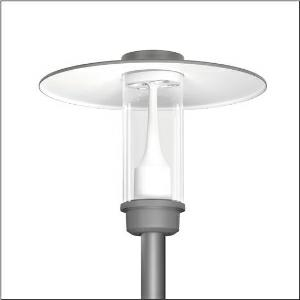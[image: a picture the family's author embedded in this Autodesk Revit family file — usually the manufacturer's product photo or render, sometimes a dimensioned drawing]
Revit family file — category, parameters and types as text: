
# Revit family: litepole_iq_2___p1_0a_5xa5425ff14h_b341
name_source: partatom
category: Lighting Fixtures
units: mm (PartAtom-declared; Revit-internal decimal feet)

## family parameters
Cut with Voids When Loaded = No
Host = Face
Light Source = No
Part Type = Normal
Room Calculation Point = No
Round Connector Dimension = Use Diameter
Shared = No

## types (1)
- --- (1 x LED, 1520 lm, 10.5 W, 3000K)
    Apparent Load = 11 VA
    CIE Flux Codes = 33 62 89 96 100
    Color Rendering = 70
    Color Temperature = 3000K
    Default Elevation = 1800 mm
    Description = Litepole iQ 2, mast luminaire, Module 540 iQ-SR, primary light control with 3 zone facetted reflector, of plastic, silver coated, highly specular, structured, primary optical cover: cover, of PMMA, transparent, light distribution: P1.0a, light emission: direct distribution, primary light characteristic: strongly asymmetric, installation type: post-top, LED, High Power LED, rated luminous flux: 1.520lm, luminous efficacy: 145lm/W, light colour: 730, colour temperature: 3000K, control gear: ECG iQ, control: Auto-Match, Temp-Guard, Lumen-Switch, Night-Set, Smart-Wire, Light-Fading, Desk-Remote (wireless, voltage-free reading and setting of iQ features in the workshop via application-optimized NFC function/RFID function), optimised constant luminous flux control (CLO 2.0), Street-Remote, presetting dimming logarithmic, with terminal, 6-pole, max. 2.5mm², mains connection: 220..240V, AC, 50/60Hz, start of lifetime: 11W, end of lifetime: 11W, reduction: 5W, luminaire housing, upper part, of aluminium, coated, Siteco® metallic grey (DB 702S), diameter: 750mm, height: 590mm, spigot size: d x l = 76 x 70mm (post-top) | with reducer (optional accessory) 60 x 70mm, post-top mast mounting element, of diecast aluminium, coated, Siteco® metallic grey (DB 702S), Module 540 iQ-SR, traffic white (RAL 9016), equipment: standard, protection rating (complete): IP65, insulation class (complete): insulation class II (safety insulation), certification: CE, ENEC, VDE, packaging unit: 1 piece

Light Distribution: P1.0a
    Height = 590 mm
    Lamp = 1 x LED
    Lamp Light Flux = 1520 lm
    Lamp Power = 10.5 W
    Lamp count = 1
    Length = 750 mm
    Luminous efficacy = 145 lm/W
    Manufacturer = Siteco
    ModVariant = No
    Model = 5XA5425FF14H
    Number of Poles = 1
    OnlyDefault = Yes
    Power Factor = 1
    Product Name = Litepole iQ 2 | P1.0a
    Product group = mast luminaire | pylon top
    ProductGroupID = 6100
    Protection Class = Protection class II
    Protection Degree = IP 65
    RLX_Detail_Level = 1
    RlxData = <blob elided: 138385 chars, md5=b43dc9ae>
    Socket = socket
    Standby Power = 0 W
    System Light Flux = 1520 lm
    System Power = 11 W
    Type Comments = factory setting: luminous flux: 100 % | dim-lin: 254 | 419 mA
    Type Image = l_1006518.jpg
    URL = http://relux.com
    VarID = @adj_112949
    Voltage = 0 V
    Weight = 0.00 kg
    Width = 0 mm  [stored 0 ft]

note: [stored X ft] marks values corroborated as IEEE doubles in the binary element streams (Revit-internal decimal feet)

## geometry (parser evidence)
native form markers: Blend x4, Sweep x12
no freeform markers — native parametric forms only
